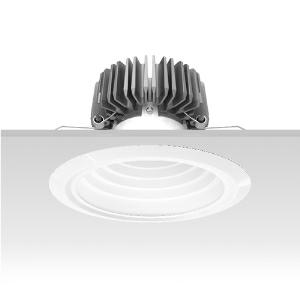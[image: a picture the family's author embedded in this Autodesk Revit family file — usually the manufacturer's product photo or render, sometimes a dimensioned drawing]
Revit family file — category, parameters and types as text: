
# Revit family: 3f_filippi_-_3f_reno_bianco_ampio_3f_filippi_-_30646_a01025_-_3f_reno_200_wh_2000-840_ep_wide___vt_wh_eef6
name_source: partatom
category: Lighting Fixtures
units: mm (PartAtom-declared; Revit-internal decimal feet)

## family parameters
Cut with Voids When Loaded = No
Host = Face
Light Source = No
Part Type = Normal
Room Calculation Point = No
Round Connector Dimension = Use Diameter
Shared = No

## types (1)
- 3F Filippi - 3F Reno Bianco Ampio (1 x LED, 1884 lm, 21 W, 4000 K)
    Apparent Load = 21 VA
    Approval mark = ENEC
    CIE Flux Codes = 75 94 99 100 100
    Color Rendering = 80
    Color Temperature = 4000 K
    Control Gear = Electronic ballast
    Default Elevation = 1800 mm
    Description = ILLUMINOTECHNICAL
Luminous efficiency 100% (DLOR 100%, ULOR 0%).
Initial luminous flux of the luminaire 1884 lm.
Emergency luminaire luminous flux BLF 20%.
Direct symmetric wide distribution.
Installation Interdistance Transv.D = 1.56 x hu - Long.D = 1.56 x hu.
Average luminance <3000 cd/m² for radial angles >65°.
Tabular UGR (CIE 117 - 4H-8H; S=0.25H; 70/50/20): RUG 20.8 - 20.6.
Beam angle: 74° - 74°.
Luminous efficacy 90 lm/W.
Lifetime (L90/B10): 30000 h. (tq+25°C)
Lifetime (L85/B10): 50000 h. (tq+25°C)
Lifetime (L70/B10): 80000 h. (tq+25°C)
Sudden decreased luminous flux after 50000 hours: 0% (C0).
Photobiological safety in compliance with IEC/TR 62778: RG0 risk exempt, (IEC 62471).
In compliance with IEC/EN 62722-2-1 - IEC/EN 62717 standards.

SOURCE
Compact LED module 2000/840.
Energy efficiency class (UE 2019/2020 - UE 2019/2015): D.
CIE 13.3 Colour rendering index: CRI >80 (R9 <50%).
IES TM-30 Fidelity Index: Rf = 84 Rg = 95.
CCT nominal colour temperature 4000 K.
Colour initial tolerance (MacAdam): SDCM 3.
Zhaga Book 3 compliant.

MECHANICAL
Passive heat dissipator in die-casting aluminium, oversized, for optimum thermal management of the LED module.
Parabolic element with graduated/concentric rings in white polycarbonate.
Transparent external lens with glossy and satin differentiated surfaces, with a cooling and anti-insect system in methacrylate (PMMA).
Fastening spring clips in stainless steel.
Dimensions: diameter 226 mm, height 146 mm. Weight 1.535 kg.
IP44 protection degree for exposed part, IP20 for recessed part.
Mechanical strength to impacts IK06 (1 joule).
Glow-wire test resistance 650°C.

ELECTRICAL
Wiring on a separate unit.
Halogen Free electronic wiring 230V-50/60Hz, power factor 0.90, THD <25%, constant output current, SELV, class II, 1 driver.
Power of the luminaire 21 W.
CE - IEC 60598-1 - EN 60598-1.
EP maintained emergency wiring on board, 1h duration, 24h recharge; compliant with EN 60598-2-22, excluding high risk areas.
SAFE FLICKER: PstLM=<1 and SVM=<0.4 (IEC TR 61547-1 and IEC TR 63158), to ensure a more comfortable and safe light.
Ambient temperature from +5°C to +25°C.
Temperature class T6 max 85°C.
Relative humidity UR: <85%.

INSTALLATION
Pull-up recessed fitting.
False ceiling carving: 200 mm.
All accessories dedicated to this product are available on the Catalog and on our website www.3F-Filippi.com.

ACCESSORIES
A01025 - VT transparent glass, tempered, not flammable, locked and in line with the trim, in white polycarbonate.

APPLICATIONS
Environments: architectural, commercial, exhibition areas, transit areas, corridors, shops, display windows, service areas.
In false ceilings with narrow voids.

WARNING
Luminaire designed for disposal/recycling at end-of-life.
Replaceable (LED only) light source by a professional. Replaceable control gear by a professional.
    Height = 0 mm  [stored 0 ft]
    Lamp = 1 x LED
    Lamp Light Flux = 1884 lm
    Lamp Power = 21 W
    Lamp count = 1
    Length = 226 mm
    Lifetime = 50000 h
    Luminous efficacy = 90 lm/W
    Manufacturer = 3F Filippi
    ModVariant = No
    Model = 3F Filippi - 30646+A01025 - 3F Reno 200 WH 2000-840 EP WIDE + VT WH
    Mounting Place = Ceiling
    Mounting Type = Recessed
    Number of Poles = 1
    OnlyDefault = Yes
    Power Factor = 1
    Product Name = 3F Filippi - 3F Reno Bianco Ampio
    Product group = recessed luminaire
    ProductGroupID = 4
    Protection Class = Protection class II
    Protection Degree = IP 20
    RLX_Detail_Level = 1
    RLX_Emergency_Light_Flux = 0 lm
    RLX_Emergency_Type = 0
    RLX_Emergency_Type_DB = No
    RlxData = <blob elided: 96093 chars, md5=503751ba>
    Socket = socket
    Standby Power = 0 W
    System Light Flux = 1884 lm
    System Power = 21 W
    Type Comments = Product without accessories
    Type Image = 3ffilippi_3f_reno_200_wh__a01025.jpg
    URL = http://relux.com
    VarID = ---
    Voltage = 0 V
    Weight = 0.00 kg
    Width = 0 mm  [stored 0 ft]

note: [stored X ft] marks values corroborated as IEEE doubles in the binary element streams (Revit-internal decimal feet)

## geometry (parser evidence)
native form markers: Blend x4, Sweep x11
no freeform markers — native parametric forms only
